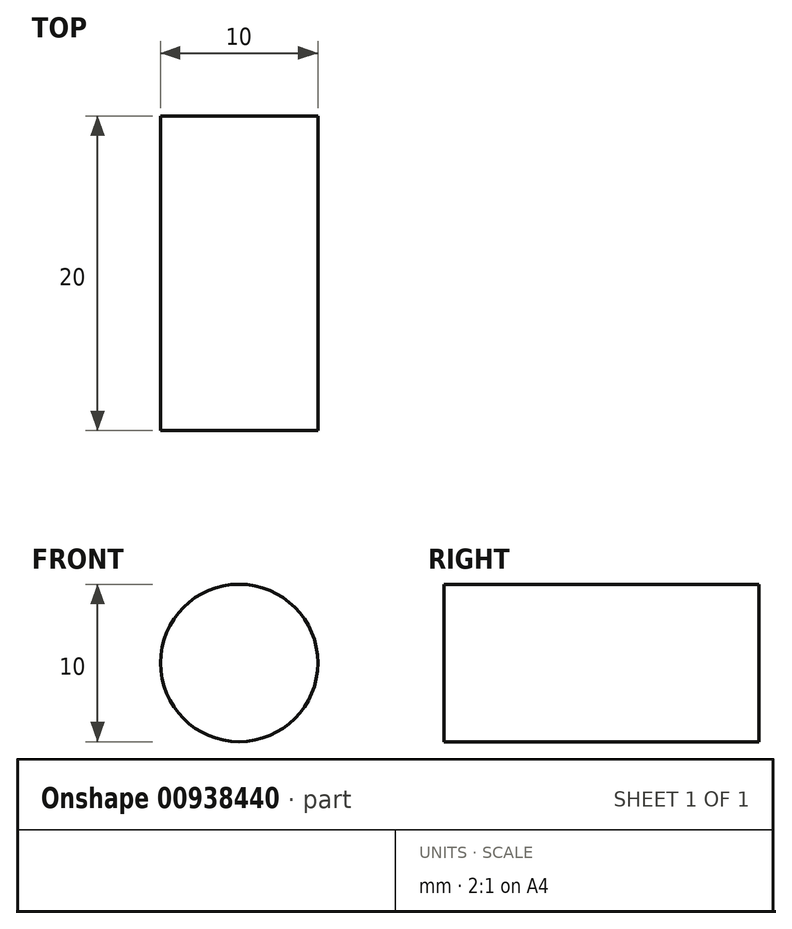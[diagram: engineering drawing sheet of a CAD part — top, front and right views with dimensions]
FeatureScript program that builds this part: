
annotation { "Feature Type Name" : "Feature", "Feature Type Description" : "" }
export const myFeature = defineFeature(function(context is Context, id is Id, definition is map)
    precondition{}
    {
        {
            var Q0;
            Q0=qCreatedBy(makeId("Front.planeOp"),FACE);
            var sketch = newSketch(context, id + "F0", { "sketchPlane" : qUnion([Q0])});
            skCircle(sketch, "E0", {"center": v(0, 0) * mm, "radius": 5 * mm});
            skSolve(sketch);
        }
        {
            var Q0;
            Q0 = qSketchRegion(id + "F0", true);
            extrude(context, id + "F1", {"entities" : qUnion([Q0]), "oppositeDirection" : true, "depth" : 20 * mm, "offsetDistance" : 25.4 * mm});
        }
    });
